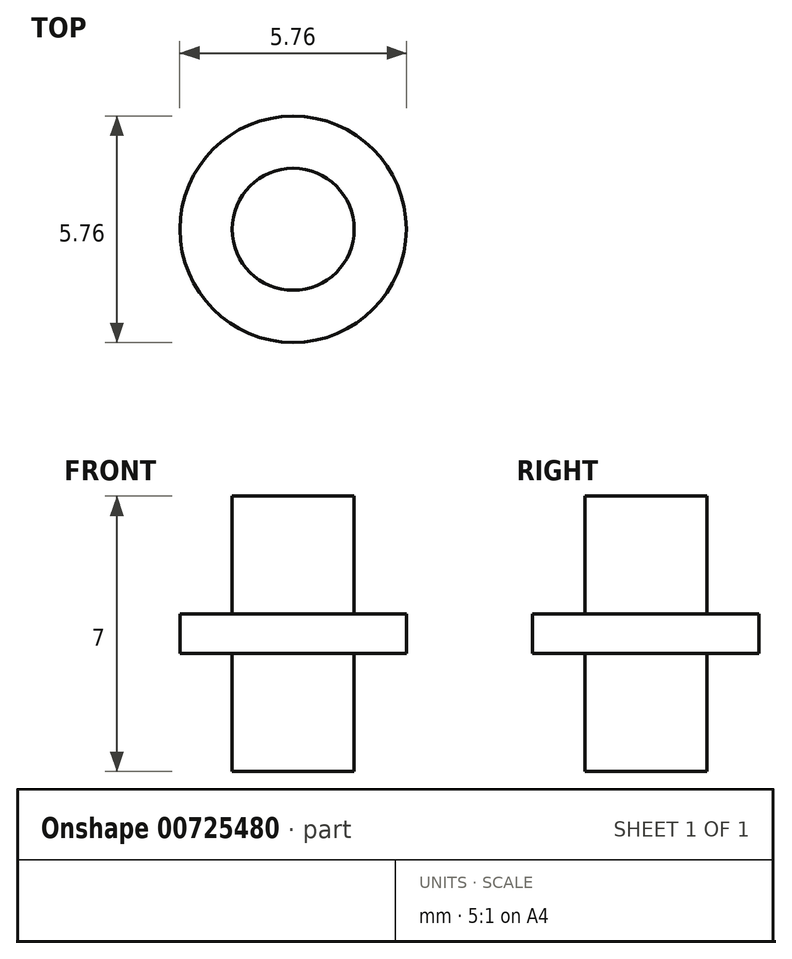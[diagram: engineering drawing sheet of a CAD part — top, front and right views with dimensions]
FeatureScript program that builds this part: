
annotation { "Feature Type Name" : "Feature", "Feature Type Description" : "" }
export const myFeature = defineFeature(function(context is Context, id is Id, definition is map)
    precondition{}
    {
        {
            var Q0;
            Q0=qCreatedBy(makeId("Top.planeOp"),FACE);
            var sketch = newSketch(context, id + "F0", { "sketchPlane" : qUnion([Q0])});
            skCircle(sketch, "E0", {"center": v(0, 0) * mm, "radius": 1.55 * mm});
            skCircle(sketch, "E1", {"center": v(0, 0) * mm, "radius": 2.88 * mm});
            skSolve(sketch);
        }
        {
            var Q0;
            Q0=makeQuery(id+"F0.imprint","IMPRINT",FACE,{"disambiguationData":[TD([[makeQuery(id+"F0.imprint","IMPRINT",EDGE,{"derivedFrom":sQuery(id+"F0.wireOp",EDGE,"E0")}),-1.0]])]});
            extrude(context, id + "F1", {"entities" : qUnion([Q0]), "endBound" : BoundingType.SYMMETRIC, "depth" : 1 * mm, "offsetDistance" : 25 * mm});
        }
        {
            var Q0;
            Q0=makeQuery(id+"F0.imprint","IMPRINT",FACE,{"disambiguationData":[TD([[makeQuery(id+"F0.imprint","IMPRINT",EDGE,{"derivedFrom":sQuery(id+"F0.wireOp",EDGE,"E0")}),1.0]])]});
            extrude(context, id + "F2", {"entities" : qUnion([Q0]), "operationType" : NewBodyOperationType.ADD, "endBound" : BoundingType.SYMMETRIC, "depth" : 7 * mm, "offsetDistance" : 25 * mm});
        }
    });
